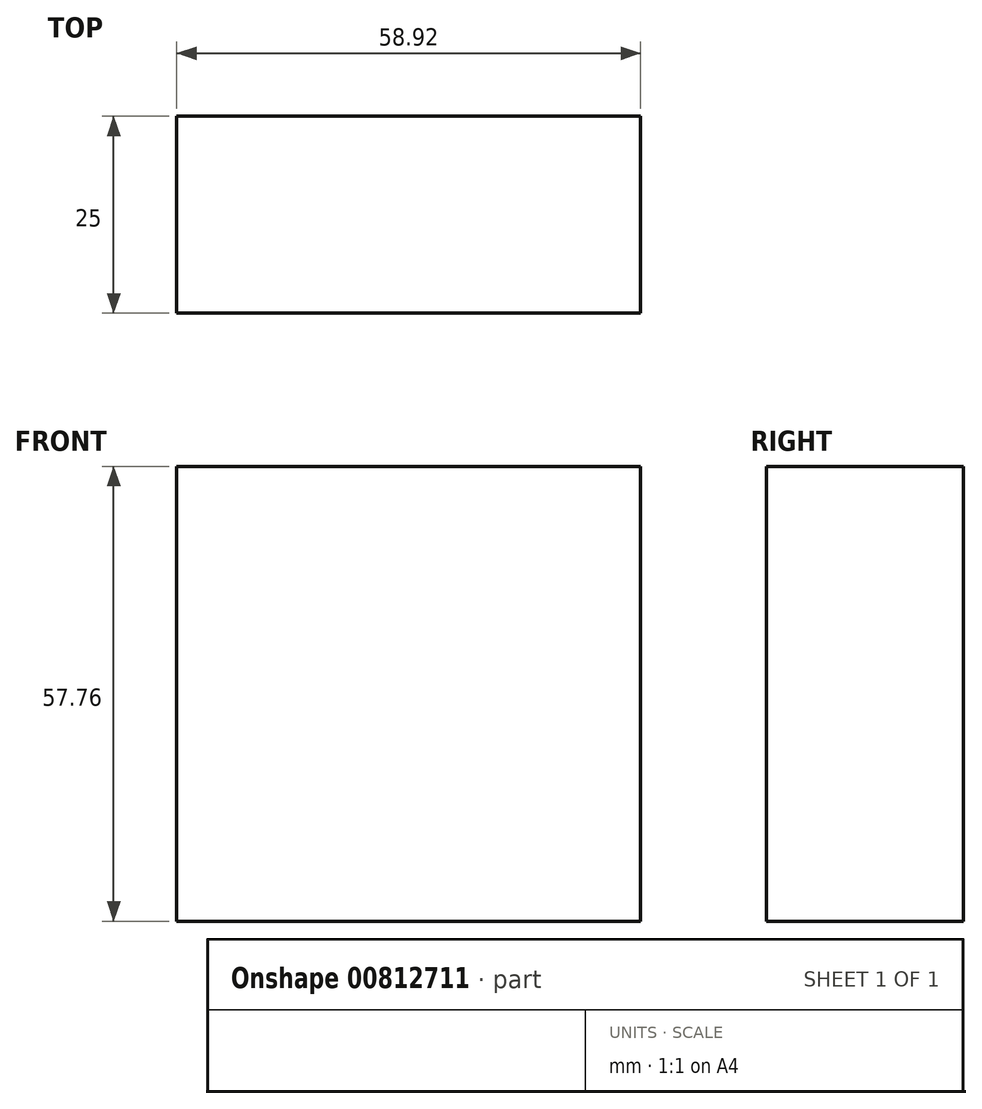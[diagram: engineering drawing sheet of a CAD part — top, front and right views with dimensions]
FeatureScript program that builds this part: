
annotation { "Feature Type Name" : "Feature", "Feature Type Description" : "" }
export const myFeature = defineFeature(function(context is Context, id is Id, definition is map)
    precondition{}
    {
        {
            var Q0;
            Q0=qCreatedBy(makeId("Front.planeOp"),FACE);
            var sketch = newSketch(context, id + "F0", { "sketchPlane" : qUnion([Q0])});
            skLineSegment(sketch, "E0.bottom", {"start": v(-61.92, 82.55) * mm, "end": v(-3, 82.55) * mm});
            skLineSegment(sketch, "E0.top", {"start": v(-61.92, 24.79) * mm, "end": v(-3, 24.79) * mm});
            skLineSegment(sketch, "E0.left", {"start": v(-61.92, 82.55) * mm, "end": v(-61.92, 24.79) * mm});
            skLineSegment(sketch, "E0.right", {"start": v(-3, 82.55) * mm, "end": v(-3, 24.79) * mm});
            skSolve(sketch);
        }
        {
            var Q0;
            Q0 = qSketchRegion(id + "F0", true);
            extrude(context, id + "F1", {"entities" : qUnion([Q0]), "depth" : 25 * mm, "offsetDistance" : 25 * mm});
        }
    });
